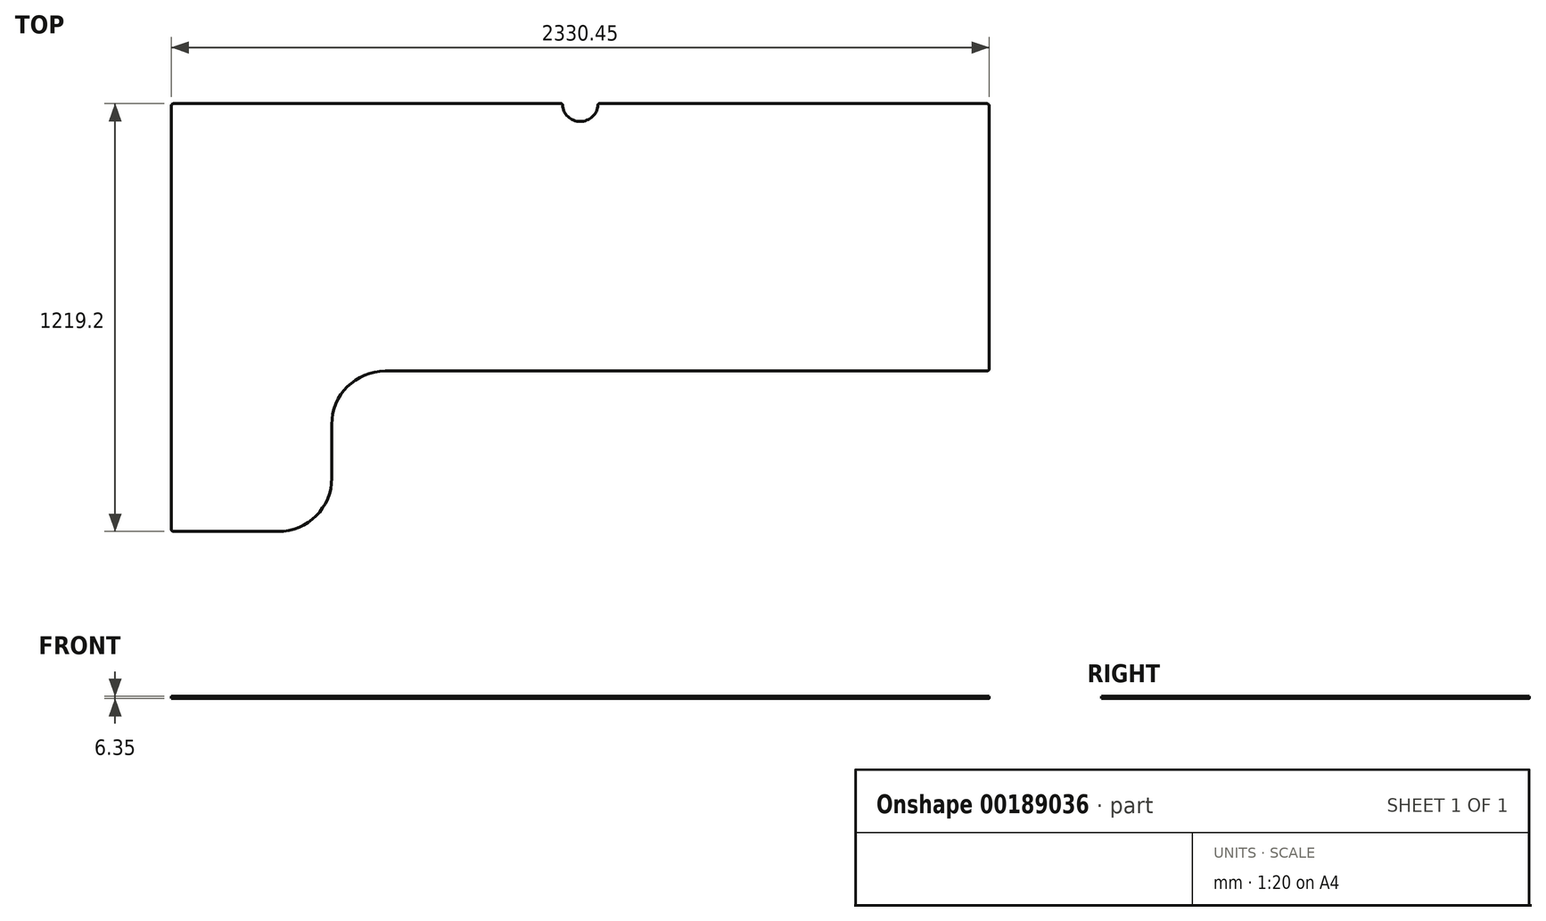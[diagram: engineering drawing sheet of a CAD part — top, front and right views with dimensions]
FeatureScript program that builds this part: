
annotation { "Feature Type Name" : "Feature", "Feature Type Description" : "" }
export const myFeature = defineFeature(function(context is Context, id is Id, definition is map)
    precondition{}
    {
        {
            var Q0;
            Q0=qCreatedBy(makeId("Top.planeOp"),FACE);
            var sketch = newSketch(context, id + "F0", { "sketchPlane" : qUnion([Q0])});
            skLineSegment(sketch, "E0.bottom", {"start": v(6.35, 0) * mm, "end": v(1111.34, 0) * mm});
            skLineSegment(sketch, "E0.top", {"start": v(6.35, -1219.2) * mm, "end": v(304.8, -1219.2) * mm});
            skLineSegment(sketch, "E0.left", {"start": v(0, -6.35) * mm, "end": v(0, -1212.85) * mm});
            skLineSegment(sketch, "E0.right", {"start": v(2330.45, -6.35) * mm, "end": v(2330.45, -755.65) * mm});
            skLineSegment(sketch, "E1", {"start": v(457.2, -1066.8) * mm, "end": v(457.2, -914.4) * mm});
            skLineSegment(sketch, "E2", {"start": v(609.6, -762) * mm, "end": v(2324.1, -762) * mm});
            skPoint(sketch, "E3.visualSharp", {"position": v(457.2, -762) * mm});
            skArc(sketch, "E3.filletArc", {"start": v(609.6, -762) * mm, "mid": v(501.84, -806.64) * mm, "end": v(457.2, -914.4) * mm});
            skArc(sketch, "E4.filletArc", {"start": v(304.8, -1219.2) * mm, "mid": v(412.56, -1174.56) * mm, "end": v(457.2, -1066.8) * mm});
            skPoint(sketch, "E5.visualSharp", {"position": v(0, -1219.2) * mm});
            skArc(sketch, "E5.filletArc", {"start": v(0, -1212.85) * mm, "mid": v(1.86, -1217.34) * mm, "end": v(6.35, -1219.2) * mm});
            skPoint(sketch, "E6.visualSharp", {"position": v(2330.45, -762) * mm});
            skArc(sketch, "E6.filletArc", {"start": v(2324.1, -762) * mm, "mid": v(2328.6, -760.14) * mm, "end": v(2330.45, -755.65) * mm});
            skPoint(sketch, "E7.visualSharp", {"position": v(2330.45, 0) * mm});
            skArc(sketch, "E7.filletArc", {"start": v(2330.45, -6.35) * mm, "mid": v(2328.6, -1.86) * mm, "end": v(2324.1, 0) * mm});
            skPoint(sketch, "E8.visualSharp", {"position": v(0, 0) * mm});
            skArc(sketch, "E8.filletArc", {"start": v(6.35, 0) * mm, "mid": v(1.86, -1.86) * mm, "end": v(0, -6.35) * mm});
            skArc(sketch, "E9", {"start": v(1114.51, -2.99) * mm, "mid": v(1165.23, -50.8) * mm, "end": v(1215.94, -2.99) * mm});
            skLineSegment(sketch, "E10.trimOffspring", {"start": v(1219.1, 0) * mm, "end": v(2324.1, 0) * mm});
            skPoint(sketch, "E11.visualSharp", {"position": v(1114.43, 0) * mm});
            skArc(sketch, "E11.filletArc", {"start": v(1114.51, -2.99) * mm, "mid": v(1113.52, -0.86) * mm, "end": v(1111.34, 0) * mm});
            skPoint(sketch, "E12.visualSharp", {"position": v(1216.03, 0) * mm});
            skArc(sketch, "E12.filletArc", {"start": v(1219.1, 0) * mm, "mid": v(1216.93, -0.86) * mm, "end": v(1215.94, -2.99) * mm});
            skSolve(sketch);
        }
        {
            var Q0;
            Q0=makeQuery(id+"F0.imprint","IMPRINT",FACE,{"disambiguationData":[TD([[makeQuery(id+"F0.imprint","IMPRINT",EDGE,{"derivedFrom":sQuery(id+"F0.wireOp",EDGE,"E0.bottom")}),-1.0]])]});
            extrude(context, id + "F1", {"entities" : qUnion([Q0]), "depth" : 6.35 * mm});
        }
    });
